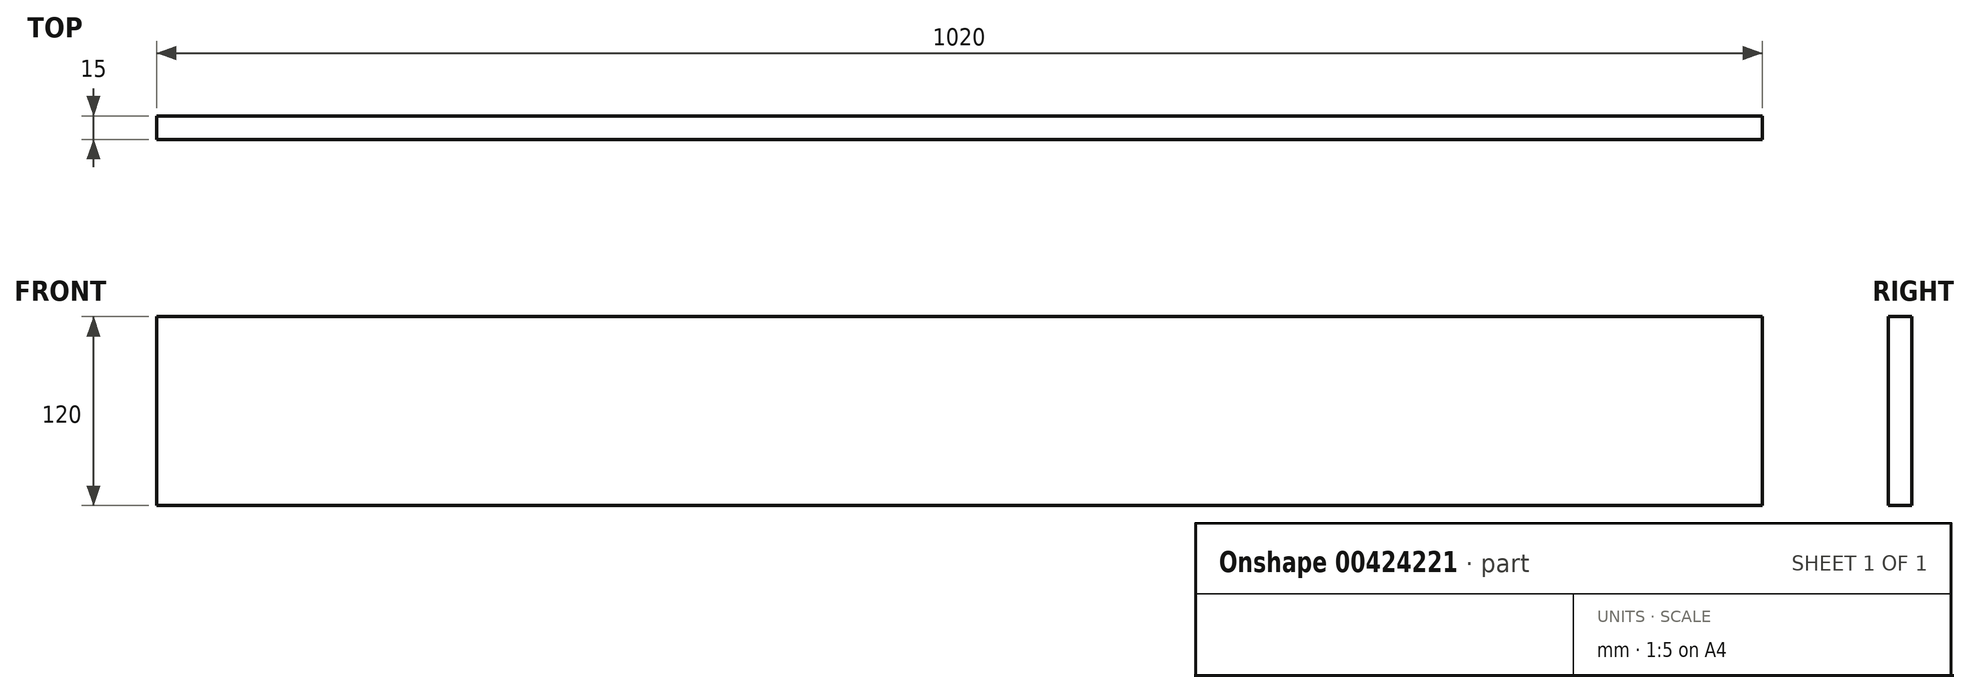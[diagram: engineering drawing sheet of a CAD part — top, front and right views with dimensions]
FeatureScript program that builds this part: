
annotation { "Feature Type Name" : "Feature", "Feature Type Description" : "" }
export const myFeature = defineFeature(function(context is Context, id is Id, definition is map)
    precondition{}
    {
        {
            var Q0;
            Q0=qCreatedBy(makeId("Front.planeOp"),FACE);
            var sketch = newSketch(context, id + "F0", { "sketchPlane" : qUnion([Q0])});
            skLineSegment(sketch, "E0.bottom", {"start": v(-515.39, -61.8) * mm, "end": v(504.61, -61.8) * mm});
            skLineSegment(sketch, "E0.top", {"start": v(-515.39, -181.8) * mm, "end": v(504.61, -181.8) * mm});
            skLineSegment(sketch, "E0.left", {"start": v(-515.39, -61.8) * mm, "end": v(-515.39, -181.8) * mm});
            skLineSegment(sketch, "E0.right", {"start": v(504.61, -61.8) * mm, "end": v(504.61, -181.8) * mm});
            skSolve(sketch);
        }
        {
            var Q0;
            Q0=makeQuery(id+"F0.imprint","IMPRINT",FACE,{"disambiguationData":[TD([[makeQuery(id+"F0.imprint","IMPRINT",EDGE,{"derivedFrom":sQuery(id+"F0.wireOp",EDGE,"E0.bottom")}),-1.0]])]});
            extrude(context, id + "F1", {"entities" : qUnion([Q0]), "depth" : 15 * mm});
        }
    });
